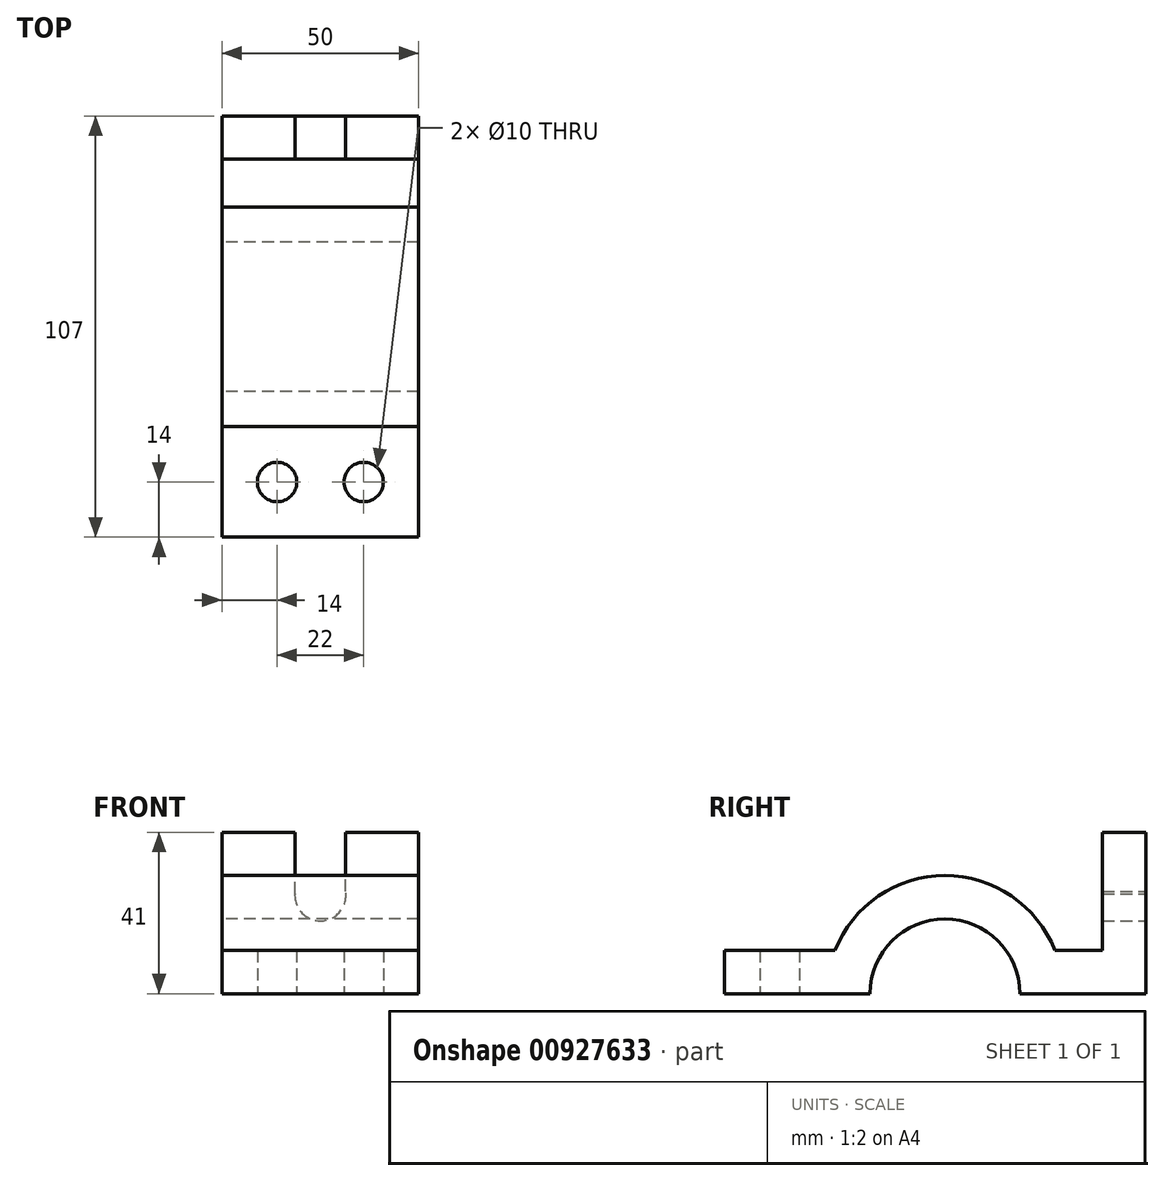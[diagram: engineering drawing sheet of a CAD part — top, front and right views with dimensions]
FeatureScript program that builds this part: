
annotation { "Feature Type Name" : "Feature", "Feature Type Description" : "" }
export const myFeature = defineFeature(function(context is Context, id is Id, definition is map)
    precondition{}
    {
        {
            var Q0;
            Q0=qCreatedBy(makeId("Right.planeOp"),FACE);
            var sketch = newSketch(context, id + "F0", { "sketchPlane" : qUnion([Q0])});
            skCircle(sketch, "E0", {"center": v(0, 0) * mm, "radius": 19 * mm});
            skCircle(sketch, "E1", {"center": v(0, 0) * mm, "radius": 30 * mm});
            skLineSegment(sketch, "E2.bottom", {"start": v(-56, 11) * mm, "end": v(51, 11) * mm});
            skLineSegment(sketch, "E2.top", {"start": v(-56, 0) * mm, "end": v(51, 0) * mm});
            skLineSegment(sketch, "E2.left", {"start": v(-56, 11) * mm, "end": v(-56, 0) * mm});
            skLineSegment(sketch, "E2.right", {"start": v(51, 11) * mm, "end": v(51, 0) * mm});
            skLineSegment(sketch, "E3.bottom", {"start": v(40, 41) * mm, "end": v(51, 41) * mm});
            skLineSegment(sketch, "E3.top", {"start": v(40, 11) * mm, "end": v(51, 11) * mm});
            skLineSegment(sketch, "E3.left", {"start": v(40, 41) * mm, "end": v(40, 11) * mm});
            skLineSegment(sketch, "E3.right", {"start": v(51, 41) * mm, "end": v(51, 11) * mm});
            skSolve(sketch);
        }
        {
            var Q0;
            Q0=makeQuery(id+"F0.imprint","IMPRINT",FACE,{"disambiguationData":[TD([[makeQuery(id+"F0.imprint","IMPRINT",EDGE,{"derivedFrom":sQuery(id+"F0.wireOp",EDGE,"E3.bottom")}),-1.0]])]});
            var Q1;
            {var subQ0=sQuery(id+"F0.wireOp",EDGE,"E2.right");Q1=makeQuery(id+"F0.imprint","IMPRINT",FACE,{"disambiguationData":[TD([[makeQuery(id+"F0.imprint","IMPRINT",EDGE,{"derivedFrom":subQ0}),-1.0]])]});}
            var Q2;
            {var subQ0=sQuery(id+"F0.wireOp",EDGE,"E2.bottom");var subQ1=sQuery(id+"F0.wireOp",EDGE,"E0");var subQ2=makeQuery(id+"F0.imprint","INTERSECT",VERTEX,{"disambiguationData":[OD(0.0)],"derivedFrom":[subQ1,subQ0]});Q2=makeQuery(id+"F0.imprint","IMPRINT",FACE,{"disambiguationData":[TD([[makeQuery(id+"F0.imprint","IMPRINT",EDGE,{"disambiguationData":[TD([[subQ2,1.0]])],"derivedFrom":subQ1}),-1.0]])]});}
            var Q3;
            {var subQ0=sQuery(id+"F0.wireOp",EDGE,"E2.bottom");var subQ1=sQuery(id+"F0.wireOp",EDGE,"E0");var subQ2=makeQuery(id+"F0.imprint","INTERSECT",VERTEX,{"disambiguationData":[OD(1.0)],"derivedFrom":[subQ1,subQ0]});Q3=makeQuery(id+"F0.imprint","IMPRINT",FACE,{"disambiguationData":[TD([[makeQuery(id+"F0.imprint","IMPRINT",EDGE,{"disambiguationData":[TD([[subQ2,1.0]])],"derivedFrom":subQ1}),-1.0]])]});}
            var Q4;
            {var subQ0=sQuery(id+"F0.wireOp",EDGE,"E2.bottom");var subQ1=sQuery(id+"F0.wireOp",EDGE,"E0");var subQ2=makeQuery(id+"F0.imprint","INTERSECT",VERTEX,{"disambiguationData":[OD(0.0)],"derivedFrom":[subQ1,subQ0]});Q4=makeQuery(id+"F0.imprint","IMPRINT",FACE,{"disambiguationData":[TD([[makeQuery(id+"F0.imprint","IMPRINT",EDGE,{"disambiguationData":[TD([[subQ2,-1.0]])],"derivedFrom":subQ1}),-1.0]])]});}
            var Q5;
            {var subQ5=sQuery(id+"F0.wireOp",EDGE,"E2.left");Q5=makeQuery(id+"F0.imprint","IMPRINT",FACE,{"disambiguationData":[TD([[makeQuery(id+"F0.imprint","IMPRINT",EDGE,{"derivedFrom":subQ5}),1.0]])]});}
            extrude(context, id + "F1", {"entities" : qUnion([Q0, Q1, Q2, Q3, Q4, Q5]), "depth" : 25 * mm, "offsetDistance" : 25 * mm});
        }
        {
            var Q0;
            Q0=makeQuery(id+"F1.opExtrude","SWEPT_BODY",BODY,{"disambiguationData":[OSD([sQuery(id+"F0.wireOp",EDGE,"E0"),sQuery(id+"F0.wireOp",EDGE,"E1"),sQuery(id+"F0.wireOp",EDGE,"E2.bottom"),sQuery(id+"F0.wireOp",EDGE,"E2.top"),sQuery(id+"F0.wireOp",EDGE,"E2.left"),sQuery(id+"F0.wireOp",EDGE,"E2.right"),sQuery(id+"F0.wireOp",EDGE,"E3.bottom"),sQuery(id+"F0.wireOp",EDGE,"E3.left"),sQuery(id+"F0.wireOp",EDGE,"E3.right")])]});
            var Q1;
            Q1=makeQuery(id+"F1.opExtrude","CAP_FACE",FACE,{"disambiguationData":[OSD([sQuery(id+"F0.wireOp",EDGE,"E0"),sQuery(id+"F0.wireOp",EDGE,"E1"),sQuery(id+"F0.wireOp",EDGE,"E2.bottom"),sQuery(id+"F0.wireOp",EDGE,"E2.top"),sQuery(id+"F0.wireOp",EDGE,"E2.left"),sQuery(id+"F0.wireOp",EDGE,"E2.right"),sQuery(id+"F0.wireOp",EDGE,"E3.bottom"),sQuery(id+"F0.wireOp",EDGE,"E3.left"),sQuery(id+"F0.wireOp",EDGE,"E3.right")])],"isStart":true});
            mirror(context, id + "F2", {"operationType" : NewBodyOperationType.ADD, "entities" : qUnion([Q0]), "mirrorPlane" : qUnion([Q1])});
        }
        {
            var Q0;
            {var subQ0=makeQuery(id+"F1.opExtrude","SWEPT_FACE",FACE,{"disambiguationData":[OSD([sQuery(id+"F0.wireOp",EDGE,"E2.right"),sQuery(id+"F0.wireOp",EDGE,"E3.right")])]});Q0=makeQuery(id+"F2.boolean.opBoolean","MERGE",FACE,{"derivedFrom":[subQ0,makeQuery(id+"F2.opPattern","COPY",FACE,{"derivedFrom":subQ0,"instanceName":"1"})]});}
            var sketch = newSketch(context, id + "F3", { "sketchPlane" : qUnion([Q0])});
            skCircle(sketch, "E4", {"center": v(0, 25) * mm, "radius": 6.5 * mm});
            skPoint(sketch, "E5", {"position": v(0, 0) * mm});
            skLineSegment(sketch, "E6", {"start": v(-6.42, 25.98) * mm, "end": v(-6.42, 41) * mm});
            skLineSegment(sketch, "E7", {"start": v(6.49, 25.38) * mm, "end": v(6.49, 41) * mm});
            skSolve(sketch);
        }
        {
            var Q0;
            Q0 = qSketchRegion(id + "F3", true);
            var Q1;
            {var subQ0=sQuery(id+"F3.wireOp",EDGE,"E6");Q1=makeQuery(id+"F3.imprint","IMPRINT",FACE,{"disambiguationData":[TD([[makeQuery(id+"F3.imprint","IMPRINT",EDGE,{"derivedFrom":subQ0}),-1.0]])]});}
            extrude(context, id + "F4", {"entities" : qUnion([Q0, Q1]), "operationType" : NewBodyOperationType.REMOVE, "oppositeDirection" : true, "depth" : 11 * mm, "offsetDistance" : 25 * mm});
        }
        {
            var Q0;
            {var subQ0=sQuery(id+"F0.wireOp",EDGE,"E2.top");var subQ2=makeQuery(id+"F1.opExtrude","SWEPT_FACE",FACE,{"disambiguationData":[OSD([subQ0]),TDD([makeQuery(id+"F0.imprint","IMPRINT",EDGE,{"disambiguationData":[TD([[makeQuery(id+"F0.imprint","INTERSECT",VERTEX,{"derivedFrom":[subQ0,sQuery(id+"F0.wireOp",EDGE,"E2.left")]}),-1.0]])],"derivedFrom":subQ0}),makeQuery(id+"F0.imprint","IMPRINT",EDGE,{"disambiguationData":[TD([[makeQuery(id+"F0.imprint","INTERSECT",VERTEX,{"disambiguationData":[OD(0.0)],"derivedFrom":[sQuery(id+"F0.wireOp",EDGE,"E0"),subQ0]}),1.0]])],"derivedFrom":subQ0})])]});Q0=makeQuery(id+"F2.boolean.opBoolean","MERGE",FACE,{"derivedFrom":[subQ2,makeQuery(id+"F2.opPattern","COPY",FACE,{"derivedFrom":subQ2,"instanceName":"1"})]});}
            var sketch = newSketch(context, id + "F5", { "sketchPlane" : qUnion([Q0])});
            skCircle(sketch, "E8", {"center": v(11, 42) * mm, "radius": 5 * mm});
            skCircle(sketch, "E9", {"center": v(-11, 42) * mm, "radius": 5 * mm});
            skSolve(sketch);
        }
        {
            var Q0;
            Q0=makeQuery(id+"F5.imprint","IMPRINT",FACE,{"disambiguationData":[TD([[makeQuery(id+"F5.imprint","IMPRINT",EDGE,{"derivedFrom":sQuery(id+"F5.wireOp",EDGE,"E9")}),1.0]])]});
            var Q1;
            Q1=makeQuery(id+"F5.imprint","IMPRINT",FACE,{"disambiguationData":[TD([[makeQuery(id+"F5.imprint","IMPRINT",EDGE,{"derivedFrom":sQuery(id+"F5.wireOp",EDGE,"E8")}),1.0]])]});
            extrude(context, id + "F6", {"entities" : qUnion([Q0, Q1]), "operationType" : NewBodyOperationType.REMOVE, "oppositeDirection" : true, "depth" : 11 * mm, "offsetDistance" : 25 * mm});
        }
    });
